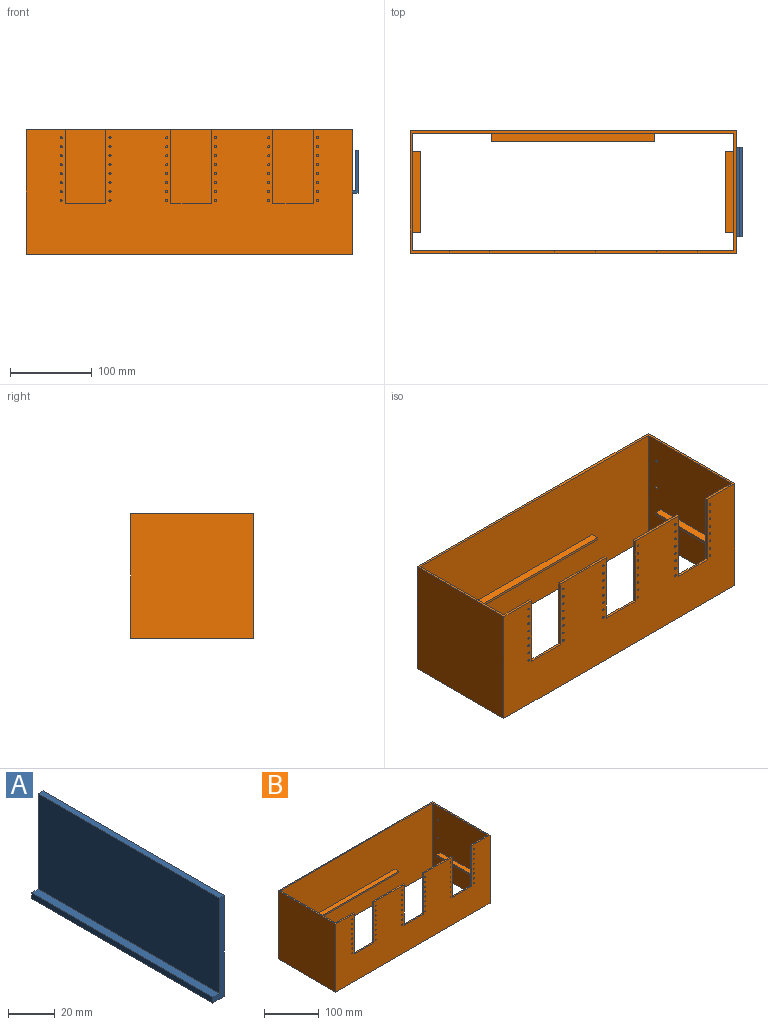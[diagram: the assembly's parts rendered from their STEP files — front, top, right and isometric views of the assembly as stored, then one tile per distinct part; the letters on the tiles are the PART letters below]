
ASSEMBLY  parts=2 mates=1
PART A: 8 faces, bbox 7x110x53 mm
  f0: plane 110x4mm, normal (0,0,1), area 440mm2, adj f1,f3,f5,f6
  f1: plane 53x7mm, normal (0,-1,0), area 171mm2, adj f0,f2,f4,f5,f6,f7
  f2: plane 110x7mm, normal (0,0,-1), area 770mm2, adj f1,f3,f4,f5
  f3: plane 53x7mm, normal (0,1,0), area 171mm2, adj f0,f2,f4,f5,f6,f7
  f4: plane 110x53mm, normal (1,0,0), area 5830mm2, adj f1,f2,f3,f7
  f5: plane 110x3mm, normal (-1,0,0), area 330mm2, adj f0,f1,f2,f3
  f6: plane 110x50mm, normal (-1,0,0), area 5500mm2, adj f0,f1,f3,f7
  f7: plane 110x3mm, normal (0,0,1), area 330mm2, adj f1,f3,f4,f6
PART B: 88 faces, bbox 400x150x153 mm
  f0: plane 79.5x3mm, normal (0,0,1), area 238.5mm2, adj f4,f7,f9,f58
  f1: plane 75x3mm, normal (0,0,1), area 225mm2, adj f2,f5,f7,f9
  f2: plane 91x3mm, normal (1,0,0), area 273mm2, adj f1,f7,f9,f86
  f3: plane 91x3mm, normal (-1,0,0), area 273mm2, adj f7,f9,f55,f86
  f4: plane 91x3mm, normal (1,0,0), area 273mm2, adj f0,f7,f9,f85
  f5: plane 91x3mm, normal (-1,0,0), area 273mm2, adj f1,f7,f9,f85
  f6: plane 400x153mm, normal (0,1,0), area 61200mm2, adj f8,f55,f56,f69
  f7: plane 400x153mm, normal (0,-1,0), area 47314.4mm2, adj f0,f1,f2,f3,f4,f5,f8,f13
  f8: plane 153x150mm, normal (1,0,0), area 22915.8mm2, adj f6,f7,f55,f65,f66,f67,f68,f69
  f9: plane 394x153mm, normal (0,1,0), area 46396.4mm2, adj f0,f1,f2,f3,f4,f5,f10,f12
  f10: plane 153x144mm, normal (1,0,0), area 21732mm2, adj f9,f11,f55,f69,f70,f71,f72,f73
  f11: plane 394x153mm, normal (0,-1,0), area 59682mm2, adj f10,f12,f55,f69,f80,f81,f82,f83
  f12: plane 153x144mm, normal (-1,0,0), area 21697.8mm2, adj f9,f11,f55,f65,f66,f67,f68,f69
  f13: cylinder r=1.25mm len=3mm, axis (0,-1,0), area 23.6mm2, adj f7,f9
  f14: cylinder r=1.25mm len=3mm, axis (0,-1,0), area 23.6mm2, adj f7,f9
  f15: cylinder r=1.25mm len=3mm, axis (0,-1,0), area 23.6mm2, adj f7,f9
  f16: cylinder r=1.25mm len=3mm, axis (0,-1,0), area 23.6mm2, adj f7,f9
  f17: cylinder r=1.25mm len=3mm, axis (0,-1,0), area 23.6mm2, adj f7,f9
  f18: cylinder r=1.25mm len=3mm, axis (0,-1,0), area 23.6mm2, adj f7,f9
  f19: cylinder r=1.25mm len=3mm, axis (0,-1,0), area 23.6mm2, adj f7,f9
  f20: cylinder r=1.25mm len=3mm, axis (0,-1,0), area 23.6mm2, adj f7,f9
  f21: cylinder r=1.25mm len=3mm, axis (0,-1,0), area 23.6mm2, adj f7,f9
  f22: cylinder r=1.25mm len=3mm, axis (0,-1,0), area 23.6mm2, adj f7,f9
  f23: cylinder r=1.25mm len=3mm, axis (0,-1,0), area 23.6mm2, adj f7,f9
  f24: cylinder r=1.25mm len=3mm, axis (0,-1,0), area 23.6mm2, adj f7,f9
  f25: cylinder r=1.25mm len=3mm, axis (0,-1,0), area 23.6mm2, adj f7,f9
  f26: cylinder r=1.25mm len=3mm, axis (0,-1,0), area 23.6mm2, adj f7,f9
  f27: cylinder r=1.25mm len=3mm, axis (0,-1,0), area 23.6mm2, adj f7,f9
  f28: cylinder r=1.25mm len=3mm, axis (0,-1,0), area 23.6mm2, adj f7,f9
  f29: cylinder r=1.25mm len=3mm, axis (0,-1,0), area 23.6mm2, adj f7,f9
  f30: cylinder r=1.25mm len=3mm, axis (0,-1,0), area 23.6mm2, adj f7,f9
  f31: cylinder r=1.25mm len=3mm, axis (0,-1,0), area 23.6mm2, adj f7,f9
  f32: cylinder r=1.25mm len=3mm, axis (0,-1,0), area 23.6mm2, adj f7,f9
  f33: cylinder r=1.25mm len=3mm, axis (0,-1,0), area 23.6mm2, adj f7,f9
  f34: cylinder r=1.25mm len=3mm, axis (0,-1,0), area 23.6mm2, adj f7,f9
  f35: cylinder r=1.25mm len=3mm, axis (0,-1,0), area 23.6mm2, adj f7,f9
  f36: cylinder r=1.25mm len=3mm, axis (0,-1,0), area 23.6mm2, adj f7,f9
  f37: cylinder r=1.25mm len=3mm, axis (0,-1,0), area 23.6mm2, adj f7,f9
  f38: cylinder r=1.25mm len=3mm, axis (0,-1,0), area 23.6mm2, adj f7,f9
  f39: cylinder r=1.25mm len=3mm, axis (0,-1,0), area 23.6mm2, adj f7,f9
  f40: cylinder r=1.25mm len=3mm, axis (0,-1,0), area 23.6mm2, adj f7,f9
  f41: cylinder r=1.25mm len=3mm, axis (0,-1,0), area 23.6mm2, adj f7,f9
  f42: cylinder r=1.25mm len=3mm, axis (0,-1,0), area 23.6mm2, adj f7,f9
  f43: cylinder r=1.25mm len=3mm, axis (0,-1,0), area 23.6mm2, adj f7,f9
  f44: cylinder r=1.25mm len=3mm, axis (0,-1,0), area 23.6mm2, adj f7,f9
  f45: cylinder r=1.25mm len=3mm, axis (0,-1,0), area 23.6mm2, adj f7,f9
  f46: cylinder r=1.25mm len=3mm, axis (0,-1,0), area 23.6mm2, adj f7,f9
  f47: cylinder r=1.25mm len=3mm, axis (0,-1,0), area 23.6mm2, adj f7,f9
  f48: cylinder r=1.25mm len=3mm, axis (0,-1,0), area 23.6mm2, adj f7,f9
  f49: cylinder r=1.25mm len=3mm, axis (0,-1,0), area 23.6mm2, adj f7,f9
  f50: cylinder r=1.25mm len=3mm, axis (0,-1,0), area 23.6mm2, adj f7,f9
  f51: cylinder r=1.25mm len=3mm, axis (0,-1,0), area 23.6mm2, adj f7,f9
  f52: cylinder r=1.25mm len=3mm, axis (0,-1,0), area 23.6mm2, adj f7,f9
  f53: cylinder r=1.25mm len=3mm, axis (0,-1,0), area 23.6mm2, adj f7,f9
  f54: cylinder r=1.25mm len=3mm, axis (0,-1,0), area 23.6mm2, adj f7,f9
  f55: plane 400x150mm, normal (0,0,1), area 2350.5mm2, adj f3,f6,f7,f8,f9,f10,f11,f12
  f56: plane 153x150mm, normal (-1,0,0), area 22950mm2, adj f6,f7,f55,f69
  f57: plane 91x3mm, normal (1,0,0), area 273mm2, adj f7,f9,f55,f87
  f58: plane 91x3mm, normal (-1,0,0), area 273mm2, adj f0,f7,f9,f87
  f59: cylinder r=1.25mm len=3mm, axis (0,-1,0), area 23.6mm2, adj f7,f9
  f60: cylinder r=1.25mm len=3mm, axis (0,-1,0), area 23.6mm2, adj f7,f9
  f61: cylinder r=1.25mm len=3mm, axis (0,-1,0), area 23.6mm2, adj f7,f9
  f62: cylinder r=1.25mm len=3mm, axis (0,-1,0), area 23.6mm2, adj f7,f9
  f63: cylinder r=1.25mm len=3mm, axis (0,-1,0), area 23.6mm2, adj f7,f9
  f64: cylinder r=1.25mm len=3mm, axis (0,-1,0), area 23.6mm2, adj f7,f9
  f65: cylinder r=1.65mm len=3.3mm, axis (1,0,0), area 31.1mm2, adj f8,f12
  f66: cylinder r=1.65mm len=3.3mm, axis (1,0,0), area 31.1mm2, adj f8,f12
  f67: cylinder r=1.65mm len=3.3mm, axis (1,0,0), area 31.1mm2, adj f8,f12
  f68: cylinder r=1.65mm len=3.3mm, axis (1,0,0), area 31.1mm2, adj f8,f12
  f69: plane 400x150mm, normal (0,0,-1), area 3264mm2, adj f6,f7,f8,f9,f10,f11,f12,f56
  f70: plane 100x10mm, normal (0,0,1), area 1000mm2, adj f10,f71,f73,f74
  f71: plane 10x3mm, normal (0,-1,0), area 30mm2, adj f10,f70,f72,f74
  f72: plane 100x10mm, normal (0,0,-1), area 1000mm2, adj f10,f71,f73,f74
  f73: plane 10x3mm, normal (0,1,0), area 30mm2, adj f10,f70,f72,f74
  f74: plane 100x3mm, normal (1,0,0), area 300mm2, adj f70,f71,f72,f73
  f75: plane 100x10mm, normal (0,0,1), area 1000mm2, adj f12,f76,f78,f79
  f76: plane 10x3mm, normal (0,1,0), area 30mm2, adj f12,f75,f77,f79
  f77: plane 100x10mm, normal (0,0,-1), area 1000mm2, adj f12,f76,f78,f79
  f78: plane 10x3mm, normal (0,-1,0), area 30mm2, adj f12,f75,f77,f79
  f79: plane 100x3mm, normal (-1,0,0), area 300mm2, adj f75,f76,f77,f78
  f80: plane 200x10mm, normal (0,0,1), area 2000mm2, adj f11,f81,f83,f84
  f81: plane 10x3mm, normal (-1,0,0), area 30mm2, adj f11,f80,f82,f84
  f82: plane 200x10mm, normal (0,0,-1), area 2000mm2, adj f11,f81,f83,f84
  f83: plane 10x3mm, normal (1,0,0), area 30mm2, adj f11,f80,f82,f84
  f84: plane 200x3mm, normal (0,-1,0), area 600mm2, adj f80,f81,f82,f83
  f85: plane 50x3mm, normal (0,0,1), area 150mm2, adj f4,f5,f7,f9
  f86: plane 50x3mm, normal (0,0,1), area 150mm2, adj f2,f3,f7,f9
  f87: plane 50x3mm, normal (0,0,1), area 150mm2, adj f7,f9,f57,f58
PLACE A t=(131.66,132.85,123.07)mm
PLACE B t=(131.66,132.85,121.11)mm
MATE fastened B.f8 <-> A.f5  axis (1,0,0) through (331.66,132.85,344.57)mm
